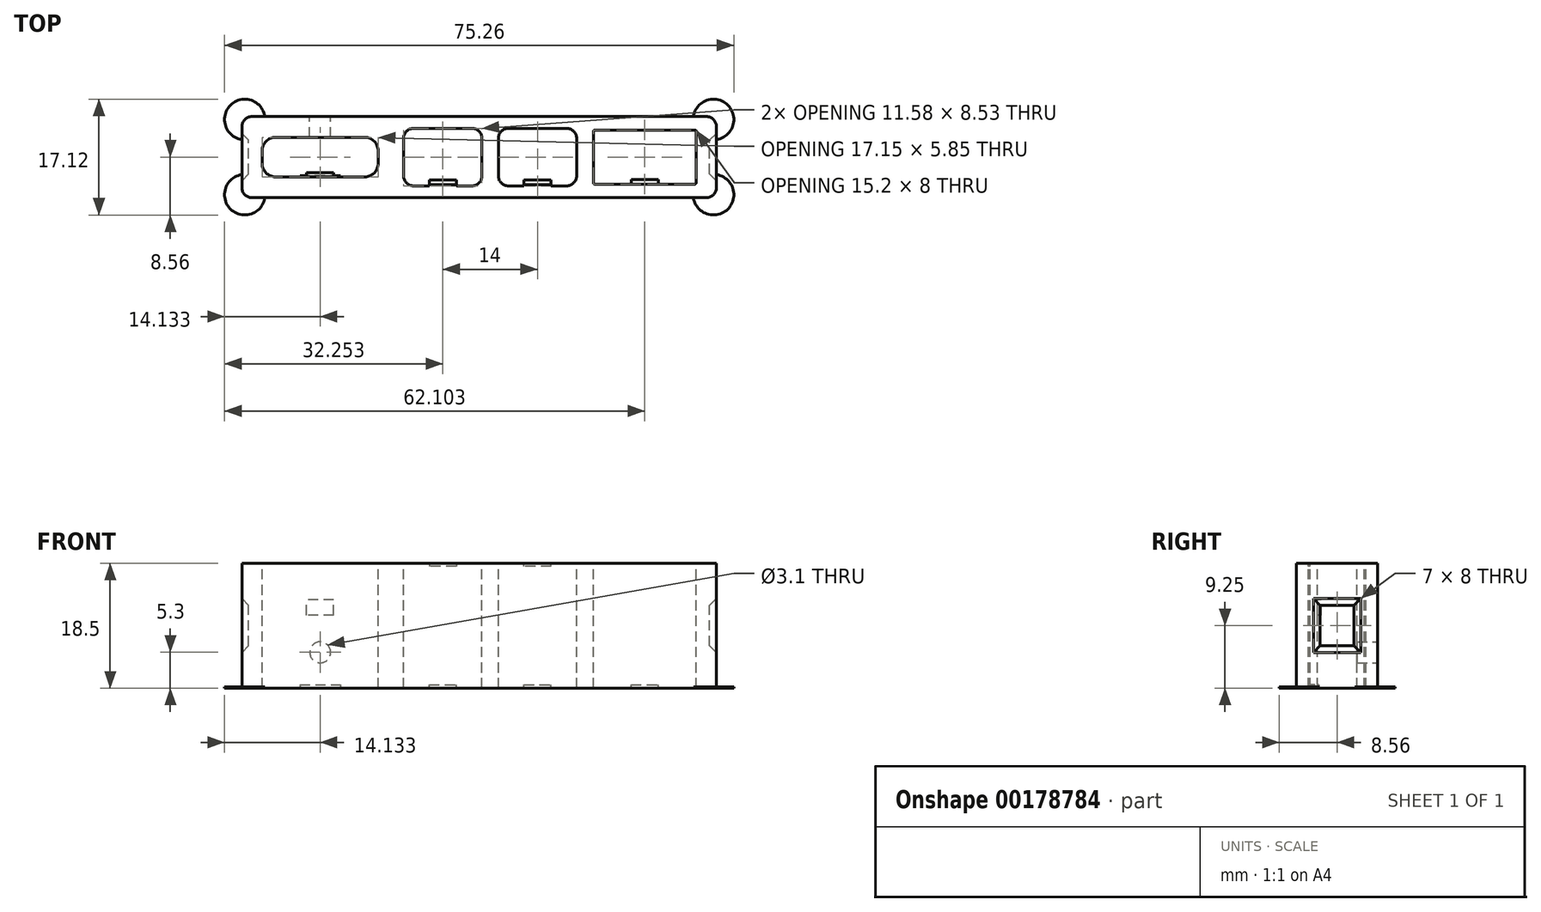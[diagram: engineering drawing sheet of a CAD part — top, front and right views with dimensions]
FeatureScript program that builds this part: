
annotation { "Feature Type Name" : "Feature", "Feature Type Description" : "" }
export const myFeature = defineFeature(function(context is Context, id is Id, definition is map)
    precondition{}
    {
        {
            assignVariable(context, id + "F0", {"name" : "TB1CableStopHeight", "anyValue" : .2});
        }
        {
            var Q0;
            Q0=qCreatedBy(makeId("Front.planeOp"),FACE);
            var sketch = newSketch(context, id + "F1", { "sketchPlane" : qUnion([Q0])});
            skLineSegment(sketch, "E0.bottom", {"start": v(33.57, -6) * mm, "end": v(-33.57, -6) * mm});
            skLineSegment(sketch, "E0.top", {"start": v(33.57, 6) * mm, "end": v(-33.57, 6) * mm});
            skLineSegment(sketch, "E0.left", {"start": v(35.07, -4.5) * mm, "end": v(35.07, 4.5) * mm});
            skLineSegment(sketch, "E0.right", {"start": v(-35.07, -4.5) * mm, "end": v(-35.07, 4.5) * mm});
            skPoint(sketch, "E0.middle", {"position": v(0, 0) * mm});
            skLineSegment(sketch, "E1", {"start": v(-35.07, 0) * mm, "end": v(35.07, 0) * mm, "construction": true});
            skLineSegment(sketch, "E2.bottom", {"start": v(-16.92, -2.92) * mm, "end": v(-30.07, -2.92) * mm});
            skLineSegment(sketch, "E2.top", {"start": v(-16.92, 2.93) * mm, "end": v(-30.07, 2.93) * mm});
            skLineSegment(sketch, "E2.left", {"start": v(-14.92, -0.92) * mm, "end": v(-14.92, 0.93) * mm});
            skLineSegment(sketch, "E2.right", {"start": v(-32.07, -0.92) * mm, "end": v(-32.07, 0.93) * mm});
            skPoint(sketch, "E2.middle", {"position": v(-23.5, 0) * mm});
            skLineSegment(sketch, "E3.bottom", {"start": v(-1.09, 4.27) * mm, "end": v(-9.67, 4.27) * mm});
            skLineSegment(sketch, "E3.top", {"start": v(-1.09, -4.26) * mm, "end": v(-9.67, -4.26) * mm});
            skLineSegment(sketch, "E3.left", {"start": v(0.41, 2.77) * mm, "end": v(0.41, -2.76) * mm});
            skLineSegment(sketch, "E3.right", {"start": v(-11.17, 2.77) * mm, "end": v(-11.17, -2.76) * mm});
            skPoint(sketch, "E3.middle", {"position": v(-5.38, 0) * mm});
            skLineSegment(sketch, "E4.bottom", {"start": v(12.91, 4.27) * mm, "end": v(4.33, 4.27) * mm});
            skLineSegment(sketch, "E4.top", {"start": v(12.91, -4.26) * mm, "end": v(4.33, -4.26) * mm});
            skLineSegment(sketch, "E4.left", {"start": v(14.41, 2.77) * mm, "end": v(14.41, -2.76) * mm});
            skLineSegment(sketch, "E4.right", {"start": v(2.83, 2.77) * mm, "end": v(2.83, -2.76) * mm});
            skPoint(sketch, "E4.middle", {"position": v(8.62, 0) * mm});
            skLineSegment(sketch, "E5.bottom", {"start": v(31.87, -4) * mm, "end": v(17.07, -4) * mm});
            skLineSegment(sketch, "E5.top", {"start": v(31.87, 4) * mm, "end": v(17.07, 4) * mm});
            skLineSegment(sketch, "E5.left", {"start": v(32.07, -3.8) * mm, "end": v(32.07, 3.8) * mm});
            skLineSegment(sketch, "E5.right", {"start": v(16.87, -3.8) * mm, "end": v(16.87, 3.8) * mm});
            skPoint(sketch, "E5.middle", {"position": v(24.47, 0) * mm});
            skPoint(sketch, "E6.visualSharp", {"position": v(-32.07, 2.93) * mm});
            skArc(sketch, "E6.filletArc", {"start": v(-30.07, 2.93) * mm, "mid": v(-31.49, 2.34) * mm, "end": v(-32.07, 0.93) * mm});
            skPoint(sketch, "E7.visualSharp", {"position": v(-14.92, 2.93) * mm});
            skArc(sketch, "E7.filletArc", {"start": v(-14.92, 0.93) * mm, "mid": v(-15.5, 2.34) * mm, "end": v(-16.92, 2.93) * mm});
            skPoint(sketch, "E8.visualSharp", {"position": v(-14.92, -2.92) * mm});
            skArc(sketch, "E8.filletArc", {"start": v(-16.92, -2.92) * mm, "mid": v(-15.5, -2.34) * mm, "end": v(-14.92, -0.92) * mm});
            skPoint(sketch, "E9.visualSharp", {"position": v(-32.07, -2.93) * mm});
            skArc(sketch, "E9.filletArc", {"start": v(-32.07, -0.92) * mm, "mid": v(-31.49, -2.34) * mm, "end": v(-30.07, -2.92) * mm});
            skPoint(sketch, "E10.visualSharp", {"position": v(-11.17, 4.27) * mm});
            skArc(sketch, "E10.filletArc", {"start": v(-9.67, 4.27) * mm, "mid": v(-10.73, 3.83) * mm, "end": v(-11.17, 2.77) * mm});
            skPoint(sketch, "E11.visualSharp", {"position": v(0.41, 4.27) * mm});
            skArc(sketch, "E11.filletArc", {"start": v(0.41, 2.77) * mm, "mid": v(-0.03, 3.83) * mm, "end": v(-1.09, 4.27) * mm});
            skPoint(sketch, "E12.visualSharp", {"position": v(-11.17, -4.26) * mm});
            skArc(sketch, "E12.filletArc", {"start": v(-11.17, -2.76) * mm, "mid": v(-10.73, -3.83) * mm, "end": v(-9.67, -4.26) * mm});
            skPoint(sketch, "E13.visualSharp", {"position": v(0.41, -4.26) * mm});
            skArc(sketch, "E13.filletArc", {"start": v(-1.09, -4.26) * mm, "mid": v(-0.03, -3.83) * mm, "end": v(0.41, -2.76) * mm});
            skPoint(sketch, "E14.visualSharp", {"position": v(2.83, 4.26) * mm});
            skArc(sketch, "E14.filletArc", {"start": v(4.33, 4.26) * mm, "mid": v(3.27, 3.83) * mm, "end": v(2.83, 2.77) * mm});
            skPoint(sketch, "E15.visualSharp", {"position": v(14.41, 4.27) * mm});
            skArc(sketch, "E15.filletArc", {"start": v(14.41, 2.77) * mm, "mid": v(13.97, 3.83) * mm, "end": v(12.91, 4.27) * mm});
            skPoint(sketch, "E16.visualSharp", {"position": v(14.41, -4.26) * mm});
            skArc(sketch, "E16.filletArc", {"start": v(12.91, -4.26) * mm, "mid": v(13.97, -3.83) * mm, "end": v(14.41, -2.76) * mm});
            skPoint(sketch, "E17.visualSharp", {"position": v(2.83, -4.26) * mm});
            skArc(sketch, "E17.filletArc", {"start": v(2.83, -2.76) * mm, "mid": v(3.27, -3.83) * mm, "end": v(4.33, -4.26) * mm});
            skPoint(sketch, "E18.visualSharp", {"position": v(16.87, 4) * mm});
            skArc(sketch, "E18.filletArc", {"start": v(17.07, 4) * mm, "mid": v(16.93, 3.94) * mm, "end": v(16.87, 3.8) * mm});
            skPoint(sketch, "E19.visualSharp", {"position": v(32.07, 4) * mm});
            skArc(sketch, "E19.filletArc", {"start": v(32.07, 3.8) * mm, "mid": v(32.01, 3.94) * mm, "end": v(31.87, 4) * mm});
            skPoint(sketch, "E20.visualSharp", {"position": v(32.07, -4) * mm});
            skArc(sketch, "E20.filletArc", {"start": v(31.87, -4) * mm, "mid": v(32.01, -3.94) * mm, "end": v(32.07, -3.8) * mm});
            skPoint(sketch, "E21.visualSharp", {"position": v(16.87, -4) * mm});
            skArc(sketch, "E21.filletArc", {"start": v(16.87, -3.8) * mm, "mid": v(16.93, -3.94) * mm, "end": v(17.07, -4) * mm});
            skPoint(sketch, "E22.visualSharp", {"position": v(-35.07, 6) * mm});
            skArc(sketch, "E22.filletArc", {"start": v(-33.57, 6) * mm, "mid": v(-34.63, 5.56) * mm, "end": v(-35.07, 4.5) * mm});
            skPoint(sketch, "E23.visualSharp", {"position": v(35.07, 6) * mm});
            skArc(sketch, "E23.filletArc", {"start": v(35.07, 4.5) * mm, "mid": v(34.63, 5.56) * mm, "end": v(33.57, 6) * mm});
            skPoint(sketch, "E24.visualSharp", {"position": v(35.07, -6) * mm});
            skArc(sketch, "E24.filletArc", {"start": v(33.57, -6) * mm, "mid": v(34.63, -5.56) * mm, "end": v(35.07, -4.5) * mm});
            skPoint(sketch, "E25.visualSharp", {"position": v(-35.07, -6) * mm});
            skArc(sketch, "E25.filletArc", {"start": v(-35.07, -4.5) * mm, "mid": v(-34.63, -5.56) * mm, "end": v(-33.57, -6) * mm});
            skSolve(sketch);
        }
        {
            var Q0;
            Q0=makeQuery(id+"F1.imprint","IMPRINT",FACE,{"disambiguationData":[TD([[makeQuery(id+"F1.imprint","IMPRINT",EDGE,{"derivedFrom":sQuery(id+"F1.wireOp",EDGE,"E0.bottom")}),-1.0]])]});
            extrude(context, id + "F2", {"entities" : qUnion([Q0]), "oppositeDirection" : true, "depth" : 18.5 * mm});
        }
        {
            var Q0;
            Q0=makeQuery(id+"F2.opExtrude","SWEPT_FACE",FACE,{"disambiguationData":[OSD([sQuery(id+"F1.wireOp",EDGE,"E0.top")])]});
            var sketch = newSketch(context, id + "F3", { "sketchPlane" : qUnion([Q0])});
            skPoint(sketch, "E26.0", {"position": v(-23.5, 0) * mm});
            skCircle(sketch, "E27", {"center": v(-23.5, 13.2) * mm, "radius": 1.55 * mm});
            skPoint(sketch, "E28.0", {"position": v(33.57, 9.25) * mm});
            skLineSegment(sketch, "E29.bottom", {"start": v(3.5, 13.25) * mm, "end": v(-3.5, 13.25) * mm});
            skLineSegment(sketch, "E29.top", {"start": v(3.5, 5.25) * mm, "end": v(-3.5, 5.25) * mm});
            skLineSegment(sketch, "E29.left", {"start": v(3.5, 13.25) * mm, "end": v(3.5, 5.25) * mm});
            skLineSegment(sketch, "E29.right", {"start": v(-3.5, 13.25) * mm, "end": v(-3.5, 5.25) * mm});
            skPoint(sketch, "E29.middle", {"position": v(0, 9.25) * mm});
            skSolve(sketch);
        }
        {
            var Q0;
            Q0=makeQuery(id+"F3.imprint","IMPRINT",FACE,{"disambiguationData":[TD([[makeQuery(id+"F3.imprint","IMPRINT",EDGE,{"derivedFrom":sQuery(id+"F3.wireOp",EDGE,"E27")}),1.0]])]});
            extrude(context, id + "F4", {"entities" : qUnion([Q0]), "operationType" : NewBodyOperationType.REMOVE, "endBound" : BoundingType.UP_TO_NEXT, "oppositeDirection" : true, "depth" : 25 * mm});
        }
        {
            var Q0;
            Q0=makeQuery(id+"F2.opExtrude","SWEPT_FACE",FACE,{"disambiguationData":[OSD([sQuery(id+"F1.wireOp",EDGE,"E2.bottom")])]});
            var sketch = newSketch(context, id + "F5", { "sketchPlane" : qUnion([Q0])});
            skPoint(sketch, "E30.0", {"position": v(-23.5, 0) * mm});
            skLineSegment(sketch, "E31.bottom", {"start": v(-26.5, 18) * mm, "end": v(-20.5, 18) * mm});
            skLineSegment(sketch, "E31.top", {"start": v(-26.5, 18.5) * mm, "end": v(-20.5, 18.5) * mm});
            skLineSegment(sketch, "E31.left", {"start": v(-26.5, 18) * mm, "end": v(-26.5, 18.5) * mm});
            skLineSegment(sketch, "E31.right", {"start": v(-20.5, 18) * mm, "end": v(-20.5, 18.5) * mm});
            skPoint(sketch, "E31.middle", {"position": v(-23.5, 18.25) * mm});
            skLineSegment(sketch, "E32.0", {"start": v(-16.92, 18.5) * mm, "end": v(-30.07, 18.5) * mm});
            skLineSegment(sketch, "E33.bottom", {"start": v(-21.5, 7.7) * mm, "end": v(-25.5, 7.7) * mm});
            skLineSegment(sketch, "E33.top", {"start": v(-21.5, 5.45) * mm, "end": v(-25.5, 5.45) * mm});
            skLineSegment(sketch, "E33.left", {"start": v(-21.5, 7.7) * mm, "end": v(-21.5, 5.45) * mm});
            skLineSegment(sketch, "E33.right", {"start": v(-25.5, 7.7) * mm, "end": v(-25.5, 5.45) * mm});
            skPoint(sketch, "E33.middle", {"position": v(-23.5, 6.57) * mm});
            skSolve(sketch);
        }
        {
            var Q0;
            Q0=makeQuery(id+"F5.imprint","IMPRINT",FACE,{"disambiguationData":[TD([[makeQuery(id+"F5.imprint","IMPRINT",EDGE,{"derivedFrom":sQuery(id+"F5.wireOp",EDGE,"E31.bottom")}),1.0]])]});
            extrude(context, id + "F6", {"entities" : qUnion([Q0]), "operationType" : NewBodyOperationType.ADD, "depth" : .2 * mm});
        }
        {
            var Q0;
            Q0=makeQuery(id+"F5.imprint","IMPRINT",FACE,{"disambiguationData":[TD([[makeQuery(id+"F5.imprint","IMPRINT",EDGE,{"derivedFrom":sQuery(id+"F5.wireOp",EDGE,"E33.bottom")}),1.0]])]});
            extrude(context, id + "F7", {"entities" : qUnion([Q0]), "operationType" : NewBodyOperationType.ADD, "depth" : .6 * mm});
        }
        {
            var Q0;
            Q0=makeQuery(id+"F2.opExtrude","SWEPT_FACE",FACE,{"disambiguationData":[OSD([sQuery(id+"F1.wireOp",EDGE,"E3.top")])]});
            var sketch = newSketch(context, id + "F8", { "sketchPlane" : qUnion([Q0])});
            skPoint(sketch, "E34.0", {"position": v(-5.38, 0) * mm});
            skLineSegment(sketch, "E35.bottom", {"start": v(-7.38, 18.5) * mm, "end": v(-3.38, 18.5) * mm});
            skLineSegment(sketch, "E35.top", {"start": v(-7.38, 18) * mm, "end": v(-3.38, 18) * mm});
            skLineSegment(sketch, "E35.left", {"start": v(-7.38, 18.5) * mm, "end": v(-7.38, 18) * mm});
            skLineSegment(sketch, "E35.right", {"start": v(-3.38, 18.5) * mm, "end": v(-3.38, 18) * mm});
            skPoint(sketch, "E35.middle", {"position": v(-5.38, 18.25) * mm});
            skLineSegment(sketch, "E36.bottom", {"start": v(-3.38, -1.03) * mm, "end": v(-7.38, -1.03) * mm});
            skLineSegment(sketch, "E36.top", {"start": v(-3.38, 0.47) * mm, "end": v(-7.38, 0.47) * mm});
            skLineSegment(sketch, "E36.left", {"start": v(-3.38, -1.03) * mm, "end": v(-3.38, 0.47) * mm});
            skLineSegment(sketch, "E36.right", {"start": v(-7.38, -1.03) * mm, "end": v(-7.38, 0.47) * mm});
            skPoint(sketch, "E36.middle", {"position": v(-5.38, -0.28) * mm});
            skLineSegment(sketch, "E37.0", {"start": v(-1.09, 18.5) * mm, "end": v(-9.67, 18.5) * mm});
            skSolve(sketch);
        }
        {
            var Q0;
            Q0=makeQuery(id+"F8.imprint","IMPRINT",FACE,{"disambiguationData":[TD([[makeQuery(id+"F8.imprint","IMPRINT",EDGE,{"derivedFrom":sQuery(id+"F8.wireOp",EDGE,"E35.top")}),1.0]])]});
            extrude(context, id + "F9", {"entities" : qUnion([Q0]), "operationType" : NewBodyOperationType.ADD, "depth" : .9 * mm});
        }
        {
            var Q0;
            {var subQ0=sQuery(id+"F8.wireOp",EDGE,"E36.top");Q0=makeQuery(id+"F8.imprint","IMPRINT",FACE,{"disambiguationData":[TD([[makeQuery(id+"F8.imprint","IMPRINT",EDGE,{"derivedFrom":subQ0}),1.0]])]});}
            extrude(context, id + "F10", {"entities" : qUnion([Q0]), "operationType" : NewBodyOperationType.ADD, "depth" : (getVariable(context, 'TB1CableStopHeight')) * mm});
        }
        {
            var Q0;
            Q0=makeQuery(id+"F2.opExtrude","SWEPT_FACE",FACE,{"disambiguationData":[OSD([sQuery(id+"F1.wireOp",EDGE,"E4.top")])]});
            var sketch = newSketch(context, id + "F11", { "sketchPlane" : qUnion([Q0])});
            skPoint(sketch, "E38.0", {"position": v(8.62, 0) * mm});
            skLineSegment(sketch, "E39.bottom", {"start": v(6.62, 18.5) * mm, "end": v(10.62, 18.5) * mm});
            skLineSegment(sketch, "E39.top", {"start": v(6.62, 18) * mm, "end": v(10.62, 18) * mm});
            skLineSegment(sketch, "E39.left", {"start": v(6.62, 18.5) * mm, "end": v(6.62, 18) * mm});
            skLineSegment(sketch, "E39.right", {"start": v(10.62, 18.5) * mm, "end": v(10.62, 18) * mm});
            skPoint(sketch, "E39.middle", {"position": v(8.62, 18.25) * mm});
            skLineSegment(sketch, "E40.bottom", {"start": v(10.62, 0.47) * mm, "end": v(6.62, 0.47) * mm});
            skLineSegment(sketch, "E40.top", {"start": v(10.62, -1.03) * mm, "end": v(6.62, -1.03) * mm});
            skLineSegment(sketch, "E40.left", {"start": v(10.62, 0.47) * mm, "end": v(10.62, -1.03) * mm});
            skLineSegment(sketch, "E40.right", {"start": v(6.62, 0.47) * mm, "end": v(6.62, -1.03) * mm});
            skPoint(sketch, "E40.middle", {"position": v(8.62, -0.28) * mm});
            skLineSegment(sketch, "E41.0", {"start": v(12.91, 18.5) * mm, "end": v(4.33, 18.5) * mm});
            skSolve(sketch);
        }
        {
            var Q0;
            Q0=makeQuery(id+"F11.imprint","IMPRINT",FACE,{"disambiguationData":[TD([[makeQuery(id+"F11.imprint","IMPRINT",EDGE,{"derivedFrom":sQuery(id+"F11.wireOp",EDGE,"E39.top")}),1.0]])]});
            extrude(context, id + "F12", {"entities" : qUnion([Q0]), "operationType" : NewBodyOperationType.ADD, "depth" : .9 * mm});
        }
        {
            var Q0;
            Q0=makeQuery(id+"F11.imprint","IMPRINT",FACE,{"disambiguationData":[TD([[makeQuery(id+"F11.imprint","IMPRINT",EDGE,{"derivedFrom":sQuery(id+"F11.wireOp",EDGE,"E40.bottom")}),1.0]])]});
            extrude(context, id + "F13", {"entities" : qUnion([Q0]), "operationType" : NewBodyOperationType.ADD, "depth" : (getVariable(context, 'TB1CableStopHeight')) * mm});
        }
        {
            var Q0;
            Q0=makeQuery(id+"F2.opExtrude","SWEPT_FACE",FACE,{"disambiguationData":[OSD([sQuery(id+"F1.wireOp",EDGE,"E5.bottom")])]});
            var sketch = newSketch(context, id + "F14", { "sketchPlane" : qUnion([Q0])});
            skPoint(sketch, "E42.0", {"position": v(24.47, 0) * mm});
            skLineSegment(sketch, "E43.bottom", {"start": v(22.47, 18.5) * mm, "end": v(26.47, 18.5) * mm});
            skLineSegment(sketch, "E43.top", {"start": v(22.47, 18) * mm, "end": v(26.47, 18) * mm});
            skLineSegment(sketch, "E43.left", {"start": v(22.47, 18.5) * mm, "end": v(22.47, 18) * mm});
            skLineSegment(sketch, "E43.right", {"start": v(26.47, 18.5) * mm, "end": v(26.47, 18) * mm});
            skPoint(sketch, "E43.middle", {"position": v(24.47, 18.25) * mm});
            skSolve(sketch);
        }
        {
            var Q0;
            Q0=makeQuery(id+"F14.imprint","IMPRINT",FACE,{"disambiguationData":[TD([[makeQuery(id+"F14.imprint","IMPRINT",EDGE,{"derivedFrom":sQuery(id+"F14.wireOp",EDGE,"E43.bottom")}),1.0]])]});
            extrude(context, id + "F15", {"entities" : qUnion([Q0]), "operationType" : NewBodyOperationType.ADD, "depth" : .7 * mm});
        }
        {
            var Q0;
            Q0=makeQuery(id+"F2.opExtrude","SWEPT_FACE",FACE,{"disambiguationData":[OSD([sQuery(id+"F1.wireOp",EDGE,"E0.left")])]});
            var sketch = newSketch(context, id + "F16", { "sketchPlane" : qUnion([Q0])});
            skPoint(sketch, "E44.0", {"position": v(9.25, 6) * mm});
            skPoint(sketch, "E45.0", {"position": v(18.5, 0) * mm});
            skLineSegment(sketch, "E46.bottom", {"start": v(13.25, 3.5) * mm, "end": v(5.25, 3.5) * mm});
            skLineSegment(sketch, "E46.top", {"start": v(13.25, -3.5) * mm, "end": v(5.25, -3.5) * mm});
            skLineSegment(sketch, "E46.left", {"start": v(13.25, 3.5) * mm, "end": v(13.25, -3.5) * mm});
            skLineSegment(sketch, "E46.right", {"start": v(5.25, 3.5) * mm, "end": v(5.25, -3.5) * mm});
            skPoint(sketch, "E46.middle", {"position": v(9.25, 0) * mm});
            skSolve(sketch);
        }
        {
            var Q0;
            Q0 = qSketchRegion(id + "F16", true);
            extrude(context, id + "F17", {"entities" : qUnion([Q0]), "operationType" : NewBodyOperationType.REMOVE, "oppositeDirection" : true, "depth" : 1 * mm, "hasDraft" : true, "draftAngle" : 45 * degree, "draftPullDirection" : true});
        }
        {
            var Q0;
            Q0=makeQuery(id+"F2.opExtrude","SWEPT_FACE",FACE,{"disambiguationData":[OSD([sQuery(id+"F1.wireOp",EDGE,"E0.right")])]});
            var sketch = newSketch(context, id + "F18", { "sketchPlane" : qUnion([Q0])});
            skPoint(sketch, "E47.0", {"position": v(-9.25, 6) * mm});
            skPoint(sketch, "E48.0", {"position": v(0, 0) * mm});
            skLineSegment(sketch, "E49.bottom", {"start": v(-5.25, -3.5) * mm, "end": v(-13.25, -3.5) * mm});
            skLineSegment(sketch, "E49.top", {"start": v(-5.25, 3.5) * mm, "end": v(-13.25, 3.5) * mm});
            skLineSegment(sketch, "E49.left", {"start": v(-5.25, -3.5) * mm, "end": v(-5.25, 3.5) * mm});
            skLineSegment(sketch, "E49.right", {"start": v(-13.25, -3.5) * mm, "end": v(-13.25, 3.5) * mm});
            skPoint(sketch, "E49.middle", {"position": v(-9.25, 0) * mm});
            skSolve(sketch);
        }
        {
            var Q0;
            Q0 = qSketchRegion(id + "F18", true);
            extrude(context, id + "F19", {"entities" : qUnion([Q0]), "operationType" : NewBodyOperationType.REMOVE, "oppositeDirection" : true, "depth" : 1 * mm, "hasDraft" : true, "draftAngle" : 45 * degree, "draftPullDirection" : true});
        }
        {
            var Q0;
            Q0=makeQuery(id+"F2.opExtrude","SWEPT_FACE",FACE,{"disambiguationData":[OSD([sQuery(id+"F1.wireOp",EDGE,"E0.bottom")])]});
            var sketch = newSketch(context, id + "F20", { "sketchPlane" : qUnion([Q0])});
            skPoint(sketch, "E50.0", {"position": v(-38.78, -17.75) * mm});
            skPoint(sketch, "E51.0", {"position": v(0, 0) * mm});
            skPoint(sketch, "E52.0", {"position": v(33.57, -9.25) * mm});
            skLineSegment(sketch, "E53.bottom", {"start": v(4, -5.75) * mm, "end": v(-4, -5.75) * mm});
            skLineSegment(sketch, "E53.top", {"start": v(4, -12.75) * mm, "end": v(-4, -12.75) * mm});
            skLineSegment(sketch, "E53.left", {"start": v(4, -5.75) * mm, "end": v(4, -12.75) * mm});
            skLineSegment(sketch, "E53.right", {"start": v(-4, -5.75) * mm, "end": v(-4, -12.75) * mm});
            skPoint(sketch, "E53.middle", {"position": v(0, -9.25) * mm});
            skText(sketch, "E54", { "text": "JS", "fontName": "OpenSans-Regular.ttf"});
            const initialGuessF20  = {"E54": [0.0279, -0.01727, 1, 0, 0.00333]};
            skSetInitialGuess(sketch, initialGuessF20);
            skSolve(sketch);
        }
        {
            var Q0;
            Q0=makeQuery(id+"F15.boolean.opBoolean","MERGE",FACE,{"derivedFrom":[makeQuery(id+"F12.boolean.opBoolean","MERGE",FACE,{"derivedFrom":[makeQuery(id+"F9.boolean.opBoolean","MERGE",FACE,{"derivedFrom":[makeQuery(id+"F6.boolean.opBoolean","MERGE",FACE,{"derivedFrom":[makeQuery(id+"F2.opExtrude","CAP_FACE",FACE,{"disambiguationData":[OSD([sQuery(id+"F1.wireOp",EDGE,"E0.bottom"),sQuery(id+"F1.wireOp",EDGE,"E0.top"),sQuery(id+"F1.wireOp",EDGE,"E0.left"),sQuery(id+"F1.wireOp",EDGE,"E0.right"),sQuery(id+"F1.wireOp",EDGE,"E2.bottom"),sQuery(id+"F1.wireOp",EDGE,"E2.top"),sQuery(id+"F1.wireOp",EDGE,"E2.left"),sQuery(id+"F1.wireOp",EDGE,"E2.right"),sQuery(id+"F1.wireOp",EDGE,"E3.bottom"),sQuery(id+"F1.wireOp",EDGE,"E3.top"),sQuery(id+"F1.wireOp",EDGE,"E3.left"),sQuery(id+"F1.wireOp",EDGE,"E3.right"),sQuery(id+"F1.wireOp",EDGE,"E4.bottom"),sQuery(id+"F1.wireOp",EDGE,"E4.top"),sQuery(id+"F1.wireOp",EDGE,"E4.left"),sQuery(id+"F1.wireOp",EDGE,"E4.right"),sQuery(id+"F1.wireOp",EDGE,"E5.bottom"),sQuery(id+"F1.wireOp",EDGE,"E5.top"),sQuery(id+"F1.wireOp",EDGE,"E5.left"),sQuery(id+"F1.wireOp",EDGE,"E5.right"),sQuery(id+"F1.wireOp",EDGE,"E6.filletArc"),sQuery(id+"F1.wireOp",EDGE,"E7.filletArc"),sQuery(id+"F1.wireOp",EDGE,"E8.filletArc"),sQuery(id+"F1.wireOp",EDGE,"E9.filletArc"),sQuery(id+"F1.wireOp",EDGE,"E10.filletArc"),sQuery(id+"F1.wireOp",EDGE,"E11.filletArc"),sQuery(id+"F1.wireOp",EDGE,"E12.filletArc"),sQuery(id+"F1.wireOp",EDGE,"E13.filletArc"),sQuery(id+"F1.wireOp",EDGE,"E14.filletArc"),sQuery(id+"F1.wireOp",EDGE,"E15.filletArc"),sQuery(id+"F1.wireOp",EDGE,"E16.filletArc"),sQuery(id+"F1.wireOp",EDGE,"E17.filletArc"),sQuery(id+"F1.wireOp",EDGE,"E18.filletArc"),sQuery(id+"F1.wireOp",EDGE,"E19.filletArc"),sQuery(id+"F1.wireOp",EDGE,"E20.filletArc"),sQuery(id+"F1.wireOp",EDGE,"E21.filletArc"),sQuery(id+"F1.wireOp",EDGE,"E22.filletArc"),sQuery(id+"F1.wireOp",EDGE,"E23.filletArc"),sQuery(id+"F1.wireOp",EDGE,"E24.filletArc"),sQuery(id+"F1.wireOp",EDGE,"E25.filletArc")])],"isStart":false}),makeQuery(id+"F6.opExtrude","SWEPT_FACE",FACE,{"disambiguationData":[OSD([sQuery(id+"F5.wireOp",EDGE,"E32.0")])]})]}),makeQuery(id+"F9.opExtrude","SWEPT_FACE",FACE,{"disambiguationData":[OSD([sQuery(id+"F8.wireOp",EDGE,"E37.0")])]})]}),makeQuery(id+"F12.opExtrude","SWEPT_FACE",FACE,{"disambiguationData":[OSD([sQuery(id+"F11.wireOp",EDGE,"E41.0")])]})]}),makeQuery(id+"F15.opExtrude","SWEPT_FACE",FACE,{"disambiguationData":[OSD([sQuery(id+"F14.wireOp",EDGE,"E43.bottom")])]})]});
            var sketch = newSketch(context, id + "F21", { "sketchPlane" : qUnion([Q0])});
            skCircle(sketch, "E55", {"center": v(-34.63, 5.56) * mm, "radius": 3 * mm});
            skCircle(sketch, "E56", {"center": v(34.63, 5.56) * mm, "radius": 3 * mm});
            skCircle(sketch, "E57", {"center": v(34.63, -5.56) * mm, "radius": 3 * mm});
            skCircle(sketch, "E58", {"center": v(-34.63, -5.56) * mm, "radius": 3 * mm});
            skSolve(sketch);
        }
        {
            var Q0;
            {var subQ5=makeQuery(id+"F2.opExtrude","CAP_EDGE",EDGE,{"disambiguationData":[OSD([sQuery(id+"F1.wireOp",EDGE,"E23.filletArc")])],"isStart":false});Q0=makeQuery(id+"F21.imprint","IMPRINT",FACE,{"disambiguationData":[TD([[makeQuery(id+"F21.imprint","IMPRINT",EDGE,{"derivedFrom":subQ5}),1.0]])]});}
            var Q1;
            {var subQ5=makeQuery(id+"F2.opExtrude","CAP_EDGE",EDGE,{"disambiguationData":[OSD([sQuery(id+"F1.wireOp",EDGE,"E24.filletArc")])],"isStart":false});Q1=makeQuery(id+"F21.imprint","IMPRINT",FACE,{"disambiguationData":[TD([[makeQuery(id+"F21.imprint","IMPRINT",EDGE,{"derivedFrom":subQ5}),1.0]])]});}
            var Q2;
            {var subQ5=makeQuery(id+"F2.opExtrude","CAP_EDGE",EDGE,{"disambiguationData":[OSD([sQuery(id+"F1.wireOp",EDGE,"E22.filletArc")])],"isStart":false});Q2=makeQuery(id+"F21.imprint","IMPRINT",FACE,{"disambiguationData":[TD([[makeQuery(id+"F21.imprint","IMPRINT",EDGE,{"derivedFrom":subQ5}),1.0]])]});}
            var Q3;
            {var subQ5=makeQuery(id+"F2.opExtrude","CAP_EDGE",EDGE,{"disambiguationData":[OSD([sQuery(id+"F1.wireOp",EDGE,"E25.filletArc")])],"isStart":false});Q3=makeQuery(id+"F21.imprint","IMPRINT",FACE,{"disambiguationData":[TD([[makeQuery(id+"F21.imprint","IMPRINT",EDGE,{"derivedFrom":subQ5}),1.0]])]});}
            extrude(context, id + "F22", {"entities" : qUnion([Q0, Q1, Q2, Q3]), "operationType" : NewBodyOperationType.ADD, "oppositeDirection" : true, "depth" : .2 * mm});
        }
        {
            var Q0;
            Q0=makeQuery(id+"F2.opExtrude","SWEPT_BODY",BODY,{"disambiguationData":[OSD([sQuery(id+"F1.wireOp",EDGE,"E0.bottom"),sQuery(id+"F1.wireOp",EDGE,"E0.top"),sQuery(id+"F1.wireOp",EDGE,"E0.left"),sQuery(id+"F1.wireOp",EDGE,"E0.right"),sQuery(id+"F1.wireOp",EDGE,"E2.bottom"),sQuery(id+"F1.wireOp",EDGE,"E2.top"),sQuery(id+"F1.wireOp",EDGE,"E2.left"),sQuery(id+"F1.wireOp",EDGE,"E2.right"),sQuery(id+"F1.wireOp",EDGE,"E3.bottom"),sQuery(id+"F1.wireOp",EDGE,"E3.top"),sQuery(id+"F1.wireOp",EDGE,"E3.left"),sQuery(id+"F1.wireOp",EDGE,"E3.right"),sQuery(id+"F1.wireOp",EDGE,"E4.bottom"),sQuery(id+"F1.wireOp",EDGE,"E4.top"),sQuery(id+"F1.wireOp",EDGE,"E4.left"),sQuery(id+"F1.wireOp",EDGE,"E4.right"),sQuery(id+"F1.wireOp",EDGE,"E5.bottom"),sQuery(id+"F1.wireOp",EDGE,"E5.top"),sQuery(id+"F1.wireOp",EDGE,"E5.left"),sQuery(id+"F1.wireOp",EDGE,"E5.right"),sQuery(id+"F1.wireOp",EDGE,"E6.filletArc"),sQuery(id+"F1.wireOp",EDGE,"E7.filletArc"),sQuery(id+"F1.wireOp",EDGE,"E8.filletArc"),sQuery(id+"F1.wireOp",EDGE,"E9.filletArc"),sQuery(id+"F1.wireOp",EDGE,"E10.filletArc"),sQuery(id+"F1.wireOp",EDGE,"E11.filletArc"),sQuery(id+"F1.wireOp",EDGE,"E12.filletArc"),sQuery(id+"F1.wireOp",EDGE,"E13.filletArc"),sQuery(id+"F1.wireOp",EDGE,"E14.filletArc"),sQuery(id+"F1.wireOp",EDGE,"E15.filletArc"),sQuery(id+"F1.wireOp",EDGE,"E16.filletArc"),sQuery(id+"F1.wireOp",EDGE,"E17.filletArc"),sQuery(id+"F1.wireOp",EDGE,"E18.filletArc"),sQuery(id+"F1.wireOp",EDGE,"E19.filletArc"),sQuery(id+"F1.wireOp",EDGE,"E20.filletArc"),sQuery(id+"F1.wireOp",EDGE,"E21.filletArc"),sQuery(id+"F1.wireOp",EDGE,"E22.filletArc"),sQuery(id+"F1.wireOp",EDGE,"E23.filletArc"),sQuery(id+"F1.wireOp",EDGE,"E24.filletArc"),sQuery(id+"F1.wireOp",EDGE,"E25.filletArc")])]});
            var Q1;
            Q1=makeQuery(id+"F2.opExtrude","CAP_EDGE",EDGE,{"disambiguationData":[OSD([sQuery(id+"F1.wireOp",EDGE,"E0.top")])],"isStart":false});
            transform(context, id + "F23", {"entities" : qUnion([Q0]), "transformType" : TransformType.ROTATION, "transformAxis" : qUnion([Q1]), "angle" : 90 * degree, "makeCopy" : false});
        }
    });
